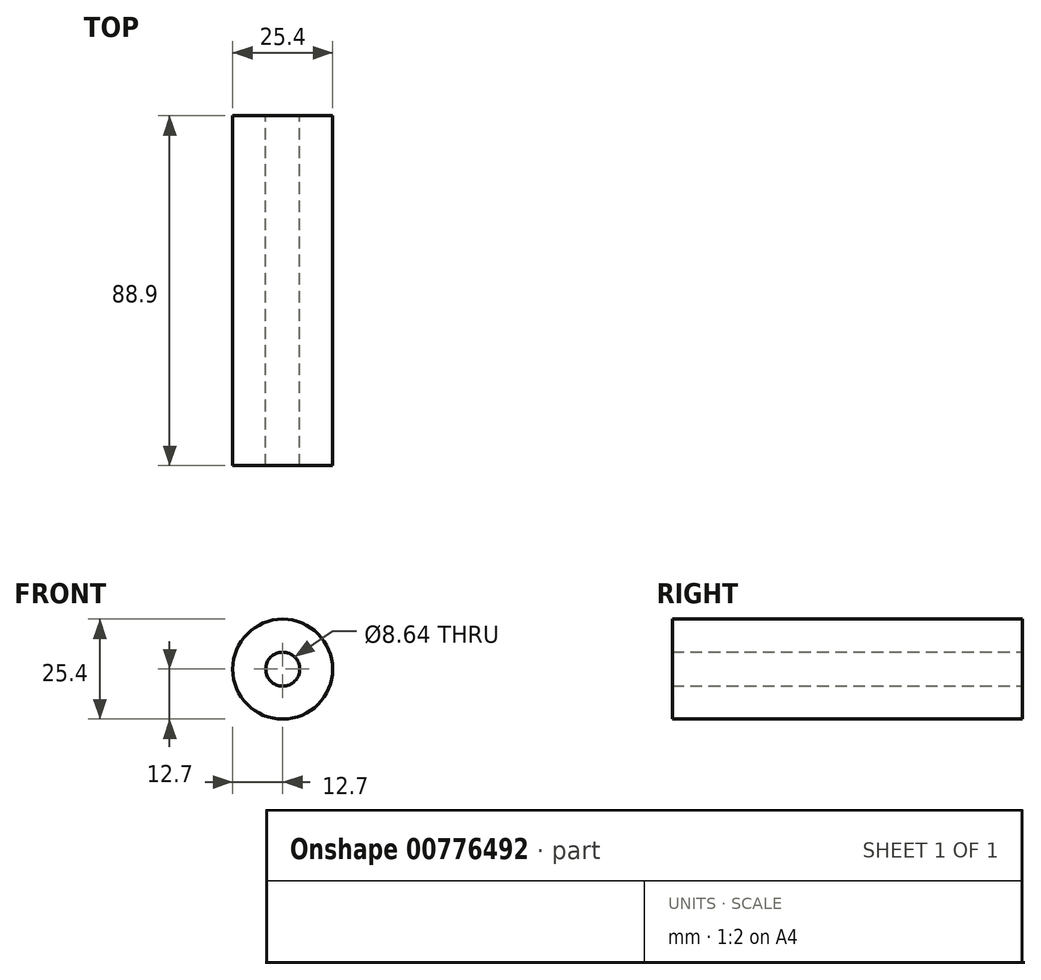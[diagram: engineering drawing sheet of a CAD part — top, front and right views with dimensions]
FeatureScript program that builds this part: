
annotation { "Feature Type Name" : "Feature", "Feature Type Description" : "" }
export const myFeature = defineFeature(function(context is Context, id is Id, definition is map)
    precondition{}
    {
        {
            var Q0;
            Q0=qCreatedBy(makeId("Front.planeOp"),FACE);
            var sketch = newSketch(context, id + "F0", { "sketchPlane" : qUnion([Q0])});
            skCircle(sketch, "E0", {"center": v(0, 0) * mm, "radius": 4.32 * mm});
            skCircle(sketch, "E1", {"center": v(0, 0) * mm, "radius": 12.7 * mm});
            skSolve(sketch);
        }
        {
            var Q0;
            Q0=qSketchRegion(id+"F0",true);
            extrude(context, id + "F1", {"entities" : qUnion([Q0]), "depth" : 88.9 * mm, "offsetDistance" : 25.4 * mm});
        }
    });
